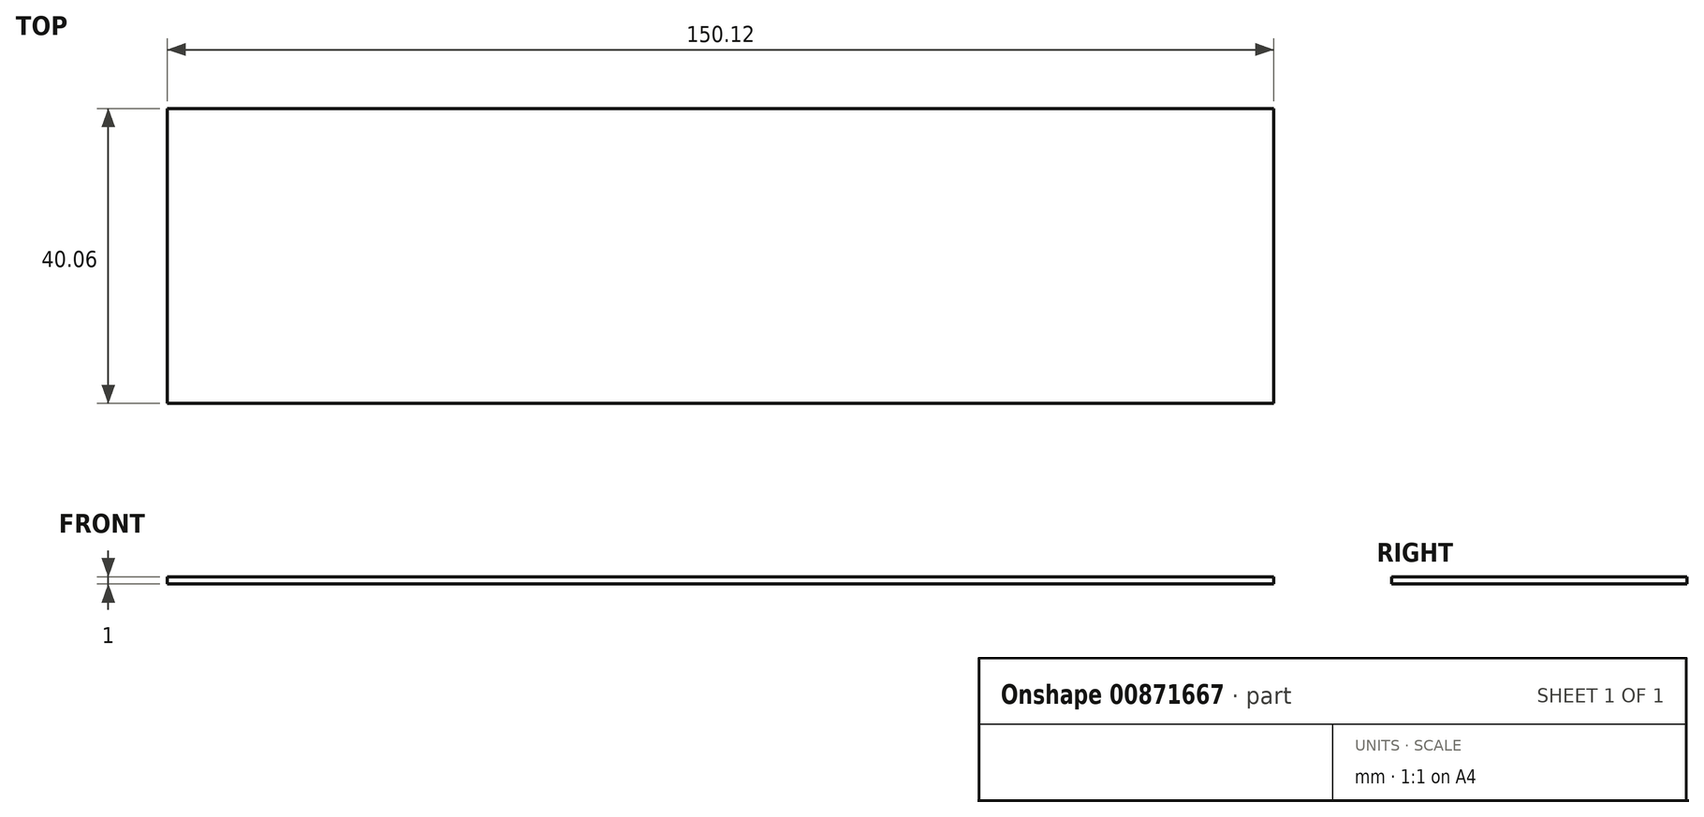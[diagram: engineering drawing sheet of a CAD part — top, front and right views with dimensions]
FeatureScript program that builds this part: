
annotation { "Feature Type Name" : "Feature", "Feature Type Description" : "" }
export const myFeature = defineFeature(function(context is Context, id is Id, definition is map)
    precondition{}
    {
        {
            var Q0;
            Q0=qCreatedBy(makeId("Top.planeOp"),FACE);
            var sketch = newSketch(context, id + "F0", { "sketchPlane" : qUnion([Q0])});
            skLineSegment(sketch, "E0.bottom", {"start": v(-130.88, 40.06) * mm, "end": v(19.24, 40.06) * mm});
            skLineSegment(sketch, "E0.top", {"start": v(-130.88, 0) * mm, "end": v(19.24, 0) * mm});
            skLineSegment(sketch, "E0.left", {"start": v(-130.88, 40.06) * mm, "end": v(-130.88, 0) * mm});
            skLineSegment(sketch, "E0.right", {"start": v(19.24, 40.06) * mm, "end": v(19.24, 0) * mm});
            skSolve(sketch);
        }
        {
            var Q0;
            Q0 = qSketchRegion(id + "F0", true);
            extrude(context, id + "F1", {"entities" : qUnion([Q0]), "depth" : 1 * mm, "offsetDistance" : 25 * mm});
        }
    });
